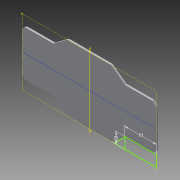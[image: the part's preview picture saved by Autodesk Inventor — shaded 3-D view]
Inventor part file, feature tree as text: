
AUTODESK INVENTOR PART (.ipt)
format: ipt  version: 2015 (Build 190159000, 159)  size: 139,264 bytes
history: native  units: mm
features: sketch x6, extrude x3, fillet x3, plane x3, mirror x2, chamfer x1
ambient origin geometry x8: Origin, YZ Plane, XZ Plane, XY Plane, X Axis, Y Axis, Z Axis, Center Point
bodies: Solid1 (feature_tree)
feature tree (18):
  extrude  "Extrusion1"  Depth=148.0mm
  sketch  "Sketch2"  dims[d2=4.0mm d3=0.0mm d4=70.0mm d5=23.0mm]
  extrude  "Extrusion2"  Depth=23.0mm
  fillet  "Fillet1"  Radius=23.0mm
  extrude  "Extrusion3"  Depth=10.0mm
  plane  "Work Plane1"
  plane  "Work Plane2"
  mirror  "Mirror2"
  fillet  "Fillet2"  Radius=10.0mm
  sketch  "Sketch5"  dims[d12=70.0mm]
  sketch  "Sketch6"  dims[d13=25.0mm d14=8.0mm d15=2.0mm d16=45.0deg d17=8.0mm]
  plane  "Work Plane3"
  mirror  "Mirror3"
  chamfer  "Chamfer1"  Distance=8.0mm Angle=45.0deg
  fillet  "Fillet3"  Radius=8.0mm
  sketch  "Sketch1"  dims[d0=300.0mm d1=148.0mm]
  sketch  "Sketch3"  dims[d6=10.0mm d7=0.0mm d8=10.0mm d9=10.0mm d10=0.0mm]
  sketch  "Sketch4"  dims[d11=10.0mm]
